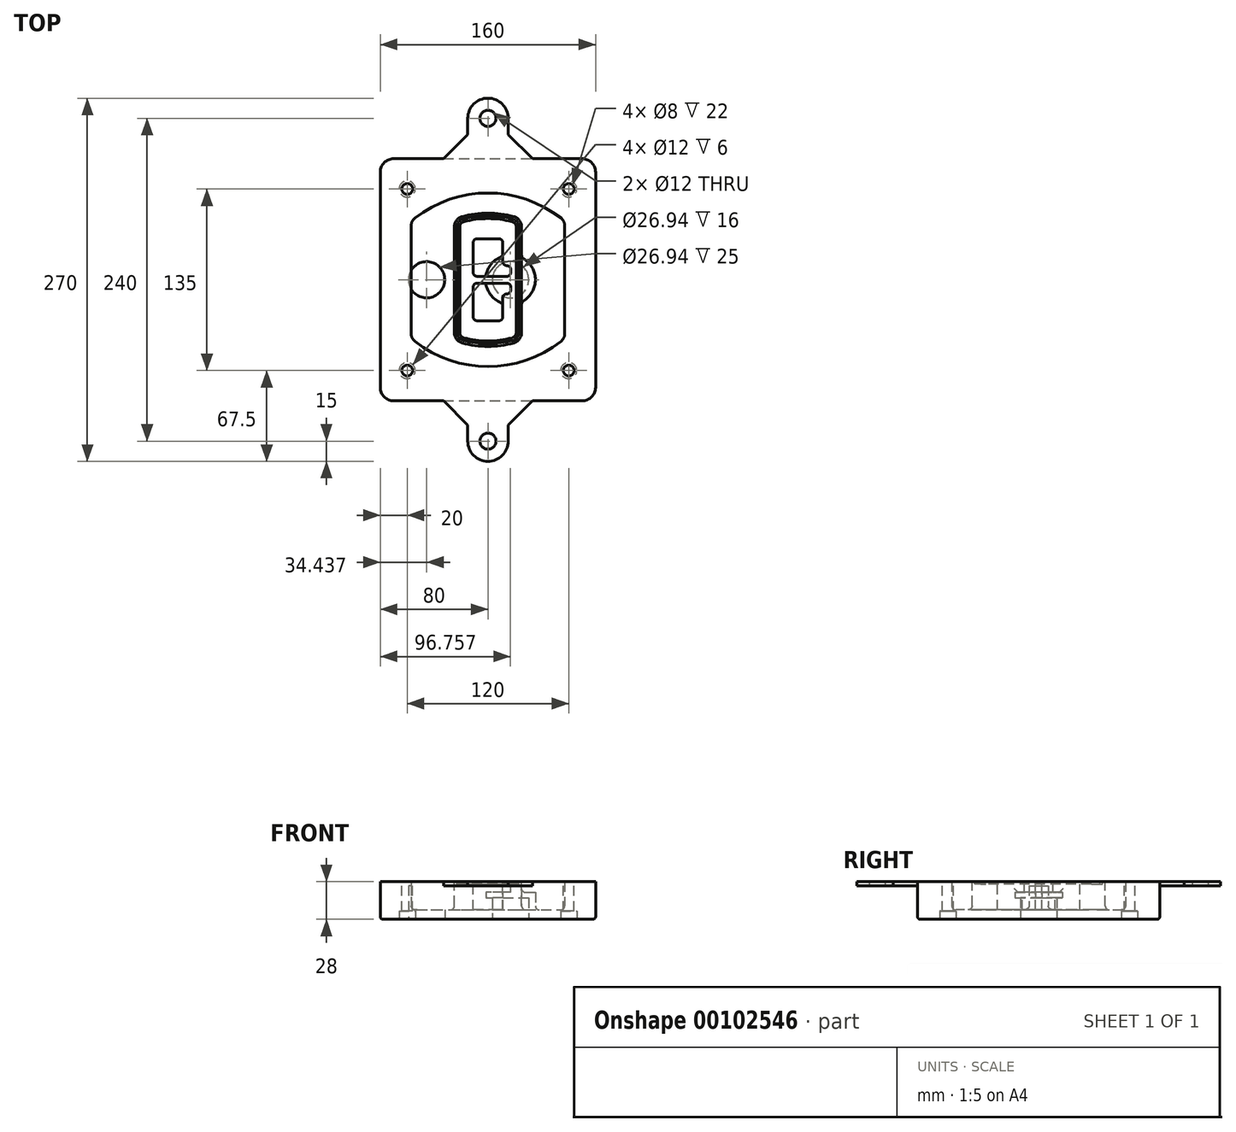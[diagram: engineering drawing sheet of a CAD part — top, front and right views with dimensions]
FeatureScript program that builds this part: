
annotation { "Feature Type Name" : "Feature", "Feature Type Description" : "" }
export const myFeature = defineFeature(function(context is Context, id is Id, definition is map)
    precondition{}
    {
        {
            var Q0;
            Q0=qCreatedBy(makeId("Top.planeOp"),FACE);
            var sketch = newSketch(context, id + "F0", { "sketchPlane" : qUnion([Q0])});
            skPoint(sketch, "E0.rect.middle", {"position": v(0, 0) * mm});
            skLineSegment(sketch, "E1.bottom", {"start": v(-70, -90) * mm, "end": v(70, -90) * mm});
            skLineSegment(sketch, "E1.top", {"start": v(-70, 90) * mm, "end": v(70, 90) * mm});
            skLineSegment(sketch, "E1.left", {"start": v(-80, -80) * mm, "end": v(-80, 80) * mm});
            skLineSegment(sketch, "E1.right", {"start": v(80, -80) * mm, "end": v(80, 80) * mm});
            skLineSegment(sketch, "E2", {"start": v(-80, 90) * mm, "end": v(80, -90) * mm, "construction": true});
            skLineSegment(sketch, "E3", {"start": v(80, 90) * mm, "end": v(-80, -90) * mm, "construction": true});
            skCircle(sketch, "E4", {"center": v(-60, 67.5) * mm, "radius": 4 * mm});
            skCircle(sketch, "E5", {"center": v(60, 67.5) * mm, "radius": 4 * mm});
            skCircle(sketch, "E6", {"center": v(60, -67.5) * mm, "radius": 4 * mm});
            skCircle(sketch, "E7", {"center": v(-60, -67.5) * mm, "radius": 4 * mm});
            skLineSegment(sketch, "E8", {"start": v(-60, 67.5) * mm, "end": v(60, 67.5) * mm, "construction": true});
            skLineSegment(sketch, "E9", {"start": v(60, 67.5) * mm, "end": v(60, -67.5) * mm, "construction": true});
            skLineSegment(sketch, "E10", {"start": v(60, -67.5) * mm, "end": v(-60, -67.5) * mm, "construction": true});
            skLineSegment(sketch, "E11", {"start": v(-60, -67.5) * mm, "end": v(-60, 67.5) * mm, "construction": true});
            skLineSegment(sketch, "E12", {"start": v(-60, 40.3) * mm, "end": v(-60, -40.3) * mm});
            skLineSegment(sketch, "E13", {"start": v(60, 40.3) * mm, "end": v(60, -40.3) * mm});
            skArc(sketch, "E14", {"start": v(56.15, 48.18) * mm, "mid": v(0, 67.5) * mm, "end": v(-56.15, 48.18) * mm});
            skArc(sketch, "E15", {"start": v(-56.15, -48.18) * mm, "mid": v(0, -67.5) * mm, "end": v(56.15, -48.18) * mm});
            skLineSegment(sketch, "E16", {"start": v(-60, 0) * mm, "end": v(60, 0) * mm, "construction": true});
            skPoint(sketch, "E17.visualSharp", {"position": v(-60, -45) * mm});
            skArc(sketch, "E17.filletArc", {"start": v(-60, -40.3) * mm, "mid": v(-58.99, -44.68) * mm, "end": v(-56.15, -48.18) * mm});
            skPoint(sketch, "E18.visualSharp", {"position": v(-60, 45) * mm});
            skArc(sketch, "E18.filletArc", {"start": v(-56.15, 48.18) * mm, "mid": v(-58.99, 44.68) * mm, "end": v(-60, 40.3) * mm});
            skPoint(sketch, "E19.visualSharp", {"position": v(60, 45) * mm});
            skArc(sketch, "E19.filletArc", {"start": v(60, 40.3) * mm, "mid": v(58.99, 44.68) * mm, "end": v(56.15, 48.18) * mm});
            skPoint(sketch, "E20.visualSharp", {"position": v(60, -45) * mm});
            skArc(sketch, "E20.filletArc", {"start": v(56.15, -48.18) * mm, "mid": v(58.99, -44.68) * mm, "end": v(60, -40.3) * mm});
            skPoint(sketch, "E21.visualSharp", {"position": v(-80, 90) * mm});
            skArc(sketch, "E21.filletArc", {"start": v(-70, 90) * mm, "mid": v(-77.07, 87.07) * mm, "end": v(-80, 80) * mm});
            skPoint(sketch, "E22.visualSharp", {"position": v(80, 90) * mm});
            skArc(sketch, "E22.filletArc", {"start": v(80, 80) * mm, "mid": v(77.07, 87.07) * mm, "end": v(70, 90) * mm});
            skPoint(sketch, "E23.visualSharp", {"position": v(80, -90) * mm});
            skArc(sketch, "E23.filletArc", {"start": v(70, -90) * mm, "mid": v(77.07, -87.07) * mm, "end": v(80, -80) * mm});
            skPoint(sketch, "E24.visualSharp", {"position": v(-80, -90) * mm});
            skArc(sketch, "E24.filletArc", {"start": v(-80, -80) * mm, "mid": v(-77.07, -87.07) * mm, "end": v(-70, -90) * mm});
            skArc(sketch, "E25.0", {"start": v(57, 40.3) * mm, "mid": v(56.3, 43.36) * mm, "end": v(54.3, 45.81) * mm});
            skLineSegment(sketch, "E25.1", {"start": v(57, 40.3) * mm, "end": v(57, -40.3) * mm});
            skArc(sketch, "E25.2", {"start": v(54.3, -45.81) * mm, "mid": v(56.3, -43.36) * mm, "end": v(57, -40.3) * mm});
            skArc(sketch, "E25.3", {"start": v(-54.3, -45.81) * mm, "mid": v(0, -64.5) * mm, "end": v(54.3, -45.81) * mm});
            skArc(sketch, "E25.4", {"start": v(-57, -40.3) * mm, "mid": v(-56.3, -43.36) * mm, "end": v(-54.3, -45.81) * mm});
            skArc(sketch, "E25.5", {"start": v(54.3, 45.81) * mm, "mid": v(0, 64.5) * mm, "end": v(-54.3, 45.81) * mm});
            skLineSegment(sketch, "E25.6", {"start": v(-57, 40.3) * mm, "end": v(-57, -40.3) * mm});
            skArc(sketch, "E25.7", {"start": v(-54.3, 45.81) * mm, "mid": v(-56.3, 43.36) * mm, "end": v(-57, 40.3) * mm});
            skArc(sketch, "E26.0", {"start": v(-58.62, 51.33) * mm, "mid": v(-62.58, 46.43) * mm, "end": v(-64, 40.3) * mm});
            skArc(sketch, "E26.1", {"start": v(58.62, 51.33) * mm, "mid": v(0, 71.5) * mm, "end": v(-58.62, 51.33) * mm});
            skArc(sketch, "E26.2", {"start": v(64, 40.3) * mm, "mid": v(62.58, 46.43) * mm, "end": v(58.62, 51.33) * mm});
            skLineSegment(sketch, "E26.3", {"start": v(64, 40.3) * mm, "end": v(64, -40.3) * mm});
            skArc(sketch, "E26.4", {"start": v(58.62, -51.33) * mm, "mid": v(62.58, -46.43) * mm, "end": v(64, -40.3) * mm});
            skLineSegment(sketch, "E26.5", {"start": v(-64, 40.3) * mm, "end": v(-64, -40.3) * mm});
            skArc(sketch, "E26.6", {"start": v(-58.62, -51.33) * mm, "mid": v(0, -71.5) * mm, "end": v(58.62, -51.33) * mm});
            skArc(sketch, "E26.7", {"start": v(-64, -40.3) * mm, "mid": v(-62.58, -46.43) * mm, "end": v(-58.62, -51.33) * mm});
            skSolve(sketch);
        }
        {
            var Q0;
            Q0=makeQuery(id+"F0.imprint","IMPRINT",FACE,{"disambiguationData":[TD([[makeQuery(id+"F0.imprint","IMPRINT",EDGE,{"derivedFrom":sQuery(id+"F0.wireOp",EDGE,"E1.bottom")}),1.0]])]});
            var Q1;
            Q1=makeQuery(id+"F0.imprint","IMPRINT",FACE,{"disambiguationData":[TD([[makeQuery(id+"F0.imprint","IMPRINT",EDGE,{"derivedFrom":sQuery(id+"F0.wireOp",EDGE,"E12")}),1.0]])]});
            var Q2;
            Q2=makeQuery(id+"F0.imprint","IMPRINT",FACE,{"disambiguationData":[TD([[makeQuery(id+"F0.imprint","IMPRINT",EDGE,{"derivedFrom":sQuery(id+"F0.wireOp",EDGE,"E25.0")}),1.0]])]});
            var Q3;
            Q3=makeQuery(id+"F0.imprint","IMPRINT",FACE,{"disambiguationData":[TD([[makeQuery(id+"F0.imprint","IMPRINT",EDGE,{"derivedFrom":sQuery(id+"F0.wireOp",EDGE,"E12")}),-1.0]])]});
            extrude(context, id + "F1", {"entities" : qUnion([Q0, Q1, Q2, Q3]), "oppositeDirection" : true, "depth" : 25 * mm});
        }
        {
            var Q0;
            Q0=makeQuery(id+"F0.imprint","IMPRINT",FACE,{"disambiguationData":[TD([[makeQuery(id+"F0.imprint","IMPRINT",EDGE,{"derivedFrom":sQuery(id+"F0.wireOp",EDGE,"E12")}),1.0]])]});
            extrude(context, id + "F2", {"entities" : qUnion([Q0]), "operationType" : NewBodyOperationType.ADD, "depth" : 3 * mm});
        }
        {
            var Q0;
            Q0=makeQuery(id+"F0.imprint","IMPRINT",FACE,{"disambiguationData":[TD([[makeQuery(id+"F0.imprint","IMPRINT",EDGE,{"derivedFrom":sQuery(id+"F0.wireOp",EDGE,"E25.0")}),1.0]])]});
            extrude(context, id + "F3", {"entities" : qUnion([Q0]), "operationType" : NewBodyOperationType.REMOVE, "oppositeDirection" : true, "depth" : 18 * mm});
        }
        {
            var Q0;
            Q0=makeQuery(id+"F2.opExtrude","CAP_FACE",FACE,{"disambiguationData":[OSD([sQuery(id+"F0.wireOp",EDGE,"E12"),sQuery(id+"F0.wireOp",EDGE,"E13"),sQuery(id+"F0.wireOp",EDGE,"E14"),sQuery(id+"F0.wireOp",EDGE,"E15"),sQuery(id+"F0.wireOp",EDGE,"E17.filletArc"),sQuery(id+"F0.wireOp",EDGE,"E18.filletArc"),sQuery(id+"F0.wireOp",EDGE,"E19.filletArc"),sQuery(id+"F0.wireOp",EDGE,"E20.filletArc"),sQuery(id+"F0.wireOp",EDGE,"E25.0"),sQuery(id+"F0.wireOp",EDGE,"E25.1"),sQuery(id+"F0.wireOp",EDGE,"E25.2"),sQuery(id+"F0.wireOp",EDGE,"E25.3"),sQuery(id+"F0.wireOp",EDGE,"E25.4"),sQuery(id+"F0.wireOp",EDGE,"E25.5"),sQuery(id+"F0.wireOp",EDGE,"E25.6"),sQuery(id+"F0.wireOp",EDGE,"E25.7")])],"isStart":false});
            var sketch = newSketch(context, id + "F4", { "sketchPlane" : qUnion([Q0])});
            skArc(sketch, "E27.0", {"start": v(-19.08, -46.97) * mm, "mid": v(0, -49.5) * mm, "end": v(19.08, -46.97) * mm});
            skArc(sketch, "E28.0", {"start": v(19.08, 46.97) * mm, "mid": v(0, 49.5) * mm, "end": v(-19.08, 46.97) * mm});
            skLineSegment(sketch, "E29", {"start": v(-25, 39.25) * mm, "end": v(-25, -39.25) * mm});
            skLineSegment(sketch, "E30", {"start": v(25, 39.25) * mm, "end": v(25, -39.25) * mm});
            skLineSegment(sketch, "E31", {"start": v(-25, 45.1) * mm, "end": v(25, 45.1) * mm, "construction": true});
            skLineSegment(sketch, "E32", {"start": v(-25, -45.1) * mm, "end": v(25, -45.1) * mm, "construction": true});
            skPoint(sketch, "E33.visualSharp", {"position": v(-25, 45.1) * mm});
            skArc(sketch, "E33.filletArc", {"start": v(-19.08, 46.97) * mm, "mid": v(-23.35, 44.11) * mm, "end": v(-25, 39.25) * mm});
            skPoint(sketch, "E34.visualSharp", {"position": v(25, 45.1) * mm});
            skArc(sketch, "E34.filletArc", {"start": v(25, 39.25) * mm, "mid": v(23.35, 44.11) * mm, "end": v(19.08, 46.97) * mm});
            skPoint(sketch, "E35.visualSharp", {"position": v(25, -45.1) * mm});
            skArc(sketch, "E35.filletArc", {"start": v(19.08, -46.97) * mm, "mid": v(23.35, -44.11) * mm, "end": v(25, -39.25) * mm});
            skPoint(sketch, "E36.visualSharp", {"position": v(-25, -45.1) * mm});
            skArc(sketch, "E36.filletArc", {"start": v(-25, -39.25) * mm, "mid": v(-23.35, -44.11) * mm, "end": v(-19.08, -46.97) * mm});
            skArc(sketch, "E37.0", {"start": v(54.3, 45.81) * mm, "mid": v(0, 64.5) * mm, "end": v(-54.3, 45.81) * mm});
            skArc(sketch, "E37.1", {"start": v(-54.3, 45.81) * mm, "mid": v(-56.3, 43.36) * mm, "end": v(-57, 40.3) * mm});
            skLineSegment(sketch, "E37.2", {"start": v(-57, 40.3) * mm, "end": v(-57, -40.3) * mm});
            skArc(sketch, "E37.3", {"start": v(-57, -40.3) * mm, "mid": v(-56.3, -43.36) * mm, "end": v(-54.3, -45.81) * mm});
            skArc(sketch, "E37.4", {"start": v(-54.3, -45.81) * mm, "mid": v(0, -64.5) * mm, "end": v(54.3, -45.81) * mm});
            skArc(sketch, "E37.5", {"start": v(54.3, -45.81) * mm, "mid": v(56.3, -43.36) * mm, "end": v(57, -40.3) * mm});
            skLineSegment(sketch, "E37.6", {"start": v(57, 40.3) * mm, "end": v(57, -40.3) * mm});
            skArc(sketch, "E37.7", {"start": v(57, 40.3) * mm, "mid": v(56.3, 43.36) * mm, "end": v(54.3, 45.81) * mm});
            skLineSegment(sketch, "E38.0", {"start": v(23, 39.25) * mm, "end": v(23, -39.25) * mm});
            skArc(sketch, "E38.1", {"start": v(18.56, -45.04) * mm, "mid": v(21.76, -42.9) * mm, "end": v(23, -39.25) * mm});
            skArc(sketch, "E38.2", {"start": v(-18.56, -45.04) * mm, "mid": v(0, -47.5) * mm, "end": v(18.56, -45.04) * mm});
            skArc(sketch, "E38.3", {"start": v(-23, -39.25) * mm, "mid": v(-21.76, -42.9) * mm, "end": v(-18.56, -45.04) * mm});
            skLineSegment(sketch, "E38.4", {"start": v(-23, 39.25) * mm, "end": v(-23, -39.25) * mm});
            skArc(sketch, "E38.5", {"start": v(23, 39.25) * mm, "mid": v(21.76, 42.9) * mm, "end": v(18.56, 45.04) * mm});
            skArc(sketch, "E38.6", {"start": v(-18.56, 45.04) * mm, "mid": v(-21.76, 42.9) * mm, "end": v(-23, 39.25) * mm});
            skArc(sketch, "E38.7", {"start": v(18.56, 45.04) * mm, "mid": v(0, 47.5) * mm, "end": v(-18.56, 45.04) * mm});
            skArc(sketch, "E39.0", {"start": v(21, 39.25) * mm, "mid": v(20.18, 41.68) * mm, "end": v(18.04, 43.1) * mm});
            skLineSegment(sketch, "E39.1", {"start": v(21, 39.25) * mm, "end": v(21, -39.25) * mm});
            skArc(sketch, "E39.2", {"start": v(18.04, -43.1) * mm, "mid": v(20.18, -41.68) * mm, "end": v(21, -39.25) * mm});
            skArc(sketch, "E39.3", {"start": v(-18.04, -43.1) * mm, "mid": v(0, -45.5) * mm, "end": v(18.04, -43.1) * mm});
            skArc(sketch, "E39.4", {"start": v(-21, -39.25) * mm, "mid": v(-20.18, -41.68) * mm, "end": v(-18.04, -43.1) * mm});
            skArc(sketch, "E39.5", {"start": v(18.04, 43.1) * mm, "mid": v(0, 45.5) * mm, "end": v(-18.04, 43.1) * mm});
            skLineSegment(sketch, "E39.6", {"start": v(-21, 39.25) * mm, "end": v(-21, -39.25) * mm});
            skArc(sketch, "E39.7", {"start": v(-18.04, 43.1) * mm, "mid": v(-20.18, 41.68) * mm, "end": v(-21, 39.25) * mm});
            skLineSegment(sketch, "E40", {"start": v(-25, 0) * mm, "end": v(25, 0) * mm, "construction": true});
            skLineSegment(sketch, "E41", {"start": v(-11, 5.5) * mm, "end": v(-11, 27.5) * mm});
            skLineSegment(sketch, "E42", {"start": v(-8, 30.5) * mm, "end": v(8, 30.5) * mm});
            skLineSegment(sketch, "E43", {"start": v(11, 27.5) * mm, "end": v(11, 13.5) * mm});
            skLineSegment(sketch, "E44", {"start": v(14, 10.5) * mm, "end": v(14, 10.5) * mm});
            skLineSegment(sketch, "E45", {"start": v(17, 7.5) * mm, "end": v(17, 5.5) * mm});
            skLineSegment(sketch, "E46", {"start": v(14, 2.5) * mm, "end": v(-8, 2.5) * mm});
            skPoint(sketch, "E47.visualSharp", {"position": v(-11, 30.5) * mm});
            skArc(sketch, "E47.filletArc", {"start": v(-8, 30.5) * mm, "mid": v(-10.12, 29.62) * mm, "end": v(-11, 27.5) * mm});
            skPoint(sketch, "E48.visualSharp", {"position": v(11, 30.5) * mm});
            skArc(sketch, "E48.filletArc", {"start": v(11, 27.5) * mm, "mid": v(10.12, 29.62) * mm, "end": v(8, 30.5) * mm});
            skPoint(sketch, "E49.visualSharp", {"position": v(11, 10.5) * mm});
            skArc(sketch, "E49.filletArc", {"start": v(11, 13.5) * mm, "mid": v(11.88, 11.38) * mm, "end": v(14, 10.5) * mm});
            skPoint(sketch, "E50.visualSharp", {"position": v(17, 10.5) * mm});
            skArc(sketch, "E50.filletArc", {"start": v(17, 7.5) * mm, "mid": v(16.12, 9.62) * mm, "end": v(14, 10.5) * mm});
            skPoint(sketch, "E51.visualSharp", {"position": v(17, 2.5) * mm});
            skArc(sketch, "E51.filletArc", {"start": v(14, 2.5) * mm, "mid": v(16.12, 3.38) * mm, "end": v(17, 5.5) * mm});
            skPoint(sketch, "E52.visualSharp", {"position": v(-11, 2.5) * mm});
            skArc(sketch, "E52.filletArc", {"start": v(-11, 5.5) * mm, "mid": v(-10.12, 3.38) * mm, "end": v(-8, 2.5) * mm});
            skLineSegment(sketch, "E53.0.MirrorCS", {"start": v(14, -2.5) * mm, "end": v(-8, -2.5) * mm});
            skArc(sketch, "E54.0.MirrorCS", {"start": v(-11, -5.5) * mm, "mid": v(-10.12, -3.38) * mm, "end": v(-8, -2.5) * mm});
            skLineSegment(sketch, "E55.0.MirrorCS", {"start": v(-11, -5.5) * mm, "end": v(-11, -27.5) * mm});
            skArc(sketch, "E56.0.MirrorCS", {"start": v(-8, -30.5) * mm, "mid": v(-10.12, -29.62) * mm, "end": v(-11, -27.5) * mm});
            skLineSegment(sketch, "E57.0.MirrorCS", {"start": v(-8, -30.5) * mm, "end": v(8, -30.5) * mm});
            skArc(sketch, "E58.0.MirrorCS", {"start": v(11, -27.5) * mm, "mid": v(10.12, -29.62) * mm, "end": v(8, -30.5) * mm});
            skLineSegment(sketch, "E59.0.MirrorCS", {"start": v(11, -27.5) * mm, "end": v(11, -13.5) * mm});
            skArc(sketch, "E60.0.MirrorCS", {"start": v(11, -13.5) * mm, "mid": v(11.88, -11.38) * mm, "end": v(14, -10.5) * mm});
            skArc(sketch, "E61.0.MirrorCS", {"start": v(17, -7.5) * mm, "mid": v(16.12, -9.62) * mm, "end": v(14, -10.5) * mm});
            skLineSegment(sketch, "E62.0.MirrorCS", {"start": v(17, -7.5) * mm, "end": v(17, -5.5) * mm});
            skArc(sketch, "E63.0.MirrorCS", {"start": v(14, -2.5) * mm, "mid": v(16.12, -3.38) * mm, "end": v(17, -5.5) * mm});
            skSolve(sketch);
        }
        {
            var Q0;
            Q0=makeQuery(id+"F4.imprint","IMPRINT",FACE,{"disambiguationData":[TD([[makeQuery(id+"F4.imprint","IMPRINT",EDGE,{"derivedFrom":sQuery(id+"F4.wireOp",EDGE,"E27.0")}),1.0]])]});
            var Q1;
            Q1=makeQuery(id+"F4.imprint","IMPRINT",FACE,{"disambiguationData":[TD([[makeQuery(id+"F4.imprint","IMPRINT",EDGE,{"derivedFrom":sQuery(id+"F4.wireOp",EDGE,"E38.0")}),-1.0]])]});
            var Q2;
            Q2=makeQuery(id+"F4.imprint","IMPRINT",FACE,{"disambiguationData":[TD([[makeQuery(id+"F4.imprint","IMPRINT",EDGE,{"derivedFrom":sQuery(id+"F4.wireOp",EDGE,"E39.0")}),1.0]])]});
            extrude(context, id + "F5", {"entities" : qUnion([Q0, Q1, Q2]), "operationType" : NewBodyOperationType.ADD, "endBound" : BoundingType.UP_TO_NEXT, "oppositeDirection" : true, "depth" : 25 * mm});
        }
        {
            var Q0;
            Q0=makeQuery(id+"F4.imprint","IMPRINT",FACE,{"disambiguationData":[TD([[makeQuery(id+"F4.imprint","IMPRINT",EDGE,{"derivedFrom":sQuery(id+"F4.wireOp",EDGE,"E38.0")}),-1.0]])]});
            extrude(context, id + "F6", {"entities" : qUnion([Q0]), "operationType" : NewBodyOperationType.REMOVE, "oppositeDirection" : true, "depth" : 2 * mm});
        }
        {
            var Q0;
            Q0=makeQuery(id+"F1.opExtrude","CAP_FACE",FACE,{"disambiguationData":[OSD([sQuery(id+"F0.wireOp",EDGE,"E1.bottom"),sQuery(id+"F0.wireOp",EDGE,"E1.top"),sQuery(id+"F0.wireOp",EDGE,"E1.left"),sQuery(id+"F0.wireOp",EDGE,"E1.right"),sQuery(id+"F0.wireOp",EDGE,"E4"),sQuery(id+"F0.wireOp",EDGE,"E5"),sQuery(id+"F0.wireOp",EDGE,"E6"),sQuery(id+"F0.wireOp",EDGE,"E7"),sQuery(id+"F0.wireOp",EDGE,"E21.filletArc"),sQuery(id+"F0.wireOp",EDGE,"E22.filletArc"),sQuery(id+"F0.wireOp",EDGE,"E23.filletArc"),sQuery(id+"F0.wireOp",EDGE,"E24.filletArc")])],"isStart":false});
            var sketch = newSketch(context, id + "F7", { "sketchPlane" : qUnion([Q0])});
            skCircle(sketch, "E64", {"center": v(16.76, 0) * mm, "radius": 13.47 * mm});
            skCircle(sketch, "E65", {"center": v(-45.56, 0) * mm, "radius": 13.47 * mm});
            skLineSegment(sketch, "E66", {"start": v(80, 0) * mm, "end": v(-80, 0) * mm});
            skCircle(sketch, "E67", {"center": v(16.76, 0) * mm, "radius": 18.47 * mm});
            skCircle(sketch, "E68", {"center": v(60, -67.5) * mm, "radius": 6 * mm});
            skCircle(sketch, "E69", {"center": v(-60, -67.5) * mm, "radius": 6 * mm});
            skCircle(sketch, "E70", {"center": v(-60, 67.5) * mm, "radius": 6 * mm});
            skCircle(sketch, "E71", {"center": v(60, 67.5) * mm, "radius": 6 * mm});
            skSolve(sketch);
        }
        {
            var Q0;
            {var subQ1=sQuery(id+"F7.wireOp",EDGE,"E66");var subQ4=sQuery(id+"F7.wireOp",EDGE,"E64");var subQ6=makeQuery(id+"F7.imprint","INTERSECT",VERTEX,{"disambiguationData":[OD(0.0)],"derivedFrom":[subQ4,subQ1]});Q0=makeQuery(id+"F7.imprint","IMPRINT",FACE,{"disambiguationData":[TD([[makeQuery(id+"F7.imprint","IMPRINT",EDGE,{"disambiguationData":[TD([[subQ6,-1.0]])],"derivedFrom":subQ4}),-1.0]])]});}
            var Q1;
            {var subQ0=sQuery(id+"F7.wireOp",EDGE,"E66");var subQ1=sQuery(id+"F7.wireOp",EDGE,"E64");var subQ3=makeQuery(id+"F7.imprint","INTERSECT",VERTEX,{"disambiguationData":[OD(0.0)],"derivedFrom":[subQ1,subQ0]});Q1=makeQuery(id+"F7.imprint","IMPRINT",FACE,{"disambiguationData":[TD([[makeQuery(id+"F7.imprint","IMPRINT",EDGE,{"disambiguationData":[TD([[subQ3,-1.0]])],"derivedFrom":subQ1}),1.0]])]});}
            var Q2;
            {var subQ0=sQuery(id+"F7.wireOp",EDGE,"E66");var subQ1=sQuery(id+"F7.wireOp",EDGE,"E64");var subQ3=makeQuery(id+"F7.imprint","INTERSECT",VERTEX,{"disambiguationData":[OD(0.0)],"derivedFrom":[subQ1,subQ0]});Q2=makeQuery(id+"F7.imprint","IMPRINT",FACE,{"disambiguationData":[TD([[makeQuery(id+"F7.imprint","IMPRINT",EDGE,{"disambiguationData":[TD([[subQ3,1.0]])],"derivedFrom":subQ1}),1.0]])]});}
            var Q3;
            {var subQ1=sQuery(id+"F7.wireOp",EDGE,"E66");var subQ4=sQuery(id+"F7.wireOp",EDGE,"E64");var subQ6=makeQuery(id+"F7.imprint","INTERSECT",VERTEX,{"disambiguationData":[OD(0.0)],"derivedFrom":[subQ4,subQ1]});Q3=makeQuery(id+"F7.imprint","IMPRINT",FACE,{"disambiguationData":[TD([[makeQuery(id+"F7.imprint","IMPRINT",EDGE,{"disambiguationData":[TD([[subQ6,1.0]])],"derivedFrom":subQ4}),-1.0]])]});}
            extrude(context, id + "F8", {"entities" : qUnion([Q0, Q1, Q2, Q3]), "operationType" : NewBodyOperationType.ADD, "oppositeDirection" : true, "depth" : 20 * mm});
        }
        {
            var Q0;
            {var subQ0=sQuery(id+"F7.wireOp",EDGE,"E66");var subQ1=sQuery(id+"F7.wireOp",EDGE,"E64");var subQ3=makeQuery(id+"F7.imprint","INTERSECT",VERTEX,{"disambiguationData":[OD(0.0)],"derivedFrom":[subQ1,subQ0]});Q0=makeQuery(id+"F7.imprint","IMPRINT",FACE,{"disambiguationData":[TD([[makeQuery(id+"F7.imprint","IMPRINT",EDGE,{"disambiguationData":[TD([[subQ3,-1.0]])],"derivedFrom":subQ1}),1.0]])]});}
            var Q1;
            {var subQ0=sQuery(id+"F7.wireOp",EDGE,"E66");var subQ1=sQuery(id+"F7.wireOp",EDGE,"E64");var subQ3=makeQuery(id+"F7.imprint","INTERSECT",VERTEX,{"disambiguationData":[OD(0.0)],"derivedFrom":[subQ1,subQ0]});Q1=makeQuery(id+"F7.imprint","IMPRINT",FACE,{"disambiguationData":[TD([[makeQuery(id+"F7.imprint","IMPRINT",EDGE,{"disambiguationData":[TD([[subQ3,1.0]])],"derivedFrom":subQ1}),1.0]])]});}
            extrude(context, id + "F9", {"entities" : qUnion([Q0, Q1]), "operationType" : NewBodyOperationType.REMOVE, "oppositeDirection" : true, "depth" : 16 * mm});
        }
        {
            var Q0;
            {var subQ0=sQuery(id+"F7.wireOp",EDGE,"E66");var subQ1=sQuery(id+"F7.wireOp",EDGE,"E65");var subQ3=makeQuery(id+"F7.imprint","INTERSECT",VERTEX,{"disambiguationData":[OD(0.0)],"derivedFrom":[subQ1,subQ0]});Q0=makeQuery(id+"F7.imprint","IMPRINT",FACE,{"disambiguationData":[TD([[makeQuery(id+"F7.imprint","IMPRINT",EDGE,{"disambiguationData":[TD([[subQ3,-1.0]])],"derivedFrom":subQ1}),1.0]])]});}
            var Q1;
            {var subQ0=sQuery(id+"F7.wireOp",EDGE,"E66");var subQ1=sQuery(id+"F7.wireOp",EDGE,"E65");var subQ3=makeQuery(id+"F7.imprint","INTERSECT",VERTEX,{"disambiguationData":[OD(0.0)],"derivedFrom":[subQ1,subQ0]});Q1=makeQuery(id+"F7.imprint","IMPRINT",FACE,{"disambiguationData":[TD([[makeQuery(id+"F7.imprint","IMPRINT",EDGE,{"disambiguationData":[TD([[subQ3,1.0]])],"derivedFrom":subQ1}),1.0]])]});}
            extrude(context, id + "F10", {"entities" : qUnion([Q0, Q1]), "operationType" : NewBodyOperationType.REMOVE, "oppositeDirection" : true, "depth" : 25 * mm});
        }
        {
            var Q0;
            Q0=makeQuery(id+"F7.imprint","IMPRINT",FACE,{"disambiguationData":[TD([[makeQuery(id+"F7.imprint","IMPRINT",EDGE,{"derivedFrom":sQuery(id+"F7.wireOp",EDGE,"E68")}),1.0]])]});
            var Q1;
            Q1=makeQuery(id+"F7.imprint","IMPRINT",FACE,{"disambiguationData":[TD([[makeQuery(id+"F7.imprint","IMPRINT",EDGE,{"derivedFrom":makeQuery(id+"F1.opExtrude","CAP_EDGE",EDGE,{"disambiguationData":[OSD([sQuery(id+"F0.wireOp",EDGE,"E5")])],"isStart":false})}),-1.0]])]});
            var Q2;
            Q2=makeQuery(id+"F7.imprint","IMPRINT",FACE,{"disambiguationData":[TD([[makeQuery(id+"F7.imprint","IMPRINT",EDGE,{"derivedFrom":sQuery(id+"F7.wireOp",EDGE,"E69")}),1.0]])]});
            var Q3;
            Q3=makeQuery(id+"F7.imprint","IMPRINT",FACE,{"disambiguationData":[TD([[makeQuery(id+"F7.imprint","IMPRINT",EDGE,{"derivedFrom":makeQuery(id+"F1.opExtrude","CAP_EDGE",EDGE,{"disambiguationData":[OSD([sQuery(id+"F0.wireOp",EDGE,"E4")])],"isStart":false})}),-1.0]])]});
            var Q4;
            Q4=makeQuery(id+"F7.imprint","IMPRINT",FACE,{"disambiguationData":[TD([[makeQuery(id+"F7.imprint","IMPRINT",EDGE,{"derivedFrom":sQuery(id+"F7.wireOp",EDGE,"E70")}),1.0]])]});
            var Q5;
            Q5=makeQuery(id+"F7.imprint","IMPRINT",FACE,{"disambiguationData":[TD([[makeQuery(id+"F7.imprint","IMPRINT",EDGE,{"derivedFrom":makeQuery(id+"F1.opExtrude","CAP_EDGE",EDGE,{"disambiguationData":[OSD([sQuery(id+"F0.wireOp",EDGE,"E7")])],"isStart":false})}),-1.0]])]});
            var Q6;
            Q6=makeQuery(id+"F7.imprint","IMPRINT",FACE,{"disambiguationData":[TD([[makeQuery(id+"F7.imprint","IMPRINT",EDGE,{"derivedFrom":sQuery(id+"F7.wireOp",EDGE,"E71")}),1.0]])]});
            var Q7;
            Q7=makeQuery(id+"F7.imprint","IMPRINT",FACE,{"disambiguationData":[TD([[makeQuery(id+"F7.imprint","IMPRINT",EDGE,{"derivedFrom":makeQuery(id+"F1.opExtrude","CAP_EDGE",EDGE,{"disambiguationData":[OSD([sQuery(id+"F0.wireOp",EDGE,"E6")])],"isStart":false})}),-1.0]])]});
            extrude(context, id + "F11", {"entities" : qUnion([Q0, Q1, Q2, Q3, Q4, Q5, Q6, Q7]), "operationType" : NewBodyOperationType.REMOVE, "oppositeDirection" : true, "depth" : 6 * mm});
        }
        {
            var Q0;
            Q0=makeQuery(id+"F9.boolean.opBoolean","COPY",FACE,{"derivedFrom":makeQuery(id+"F9.opExtrude","CAP_FACE",FACE,{"disambiguationData":[OSD([sQuery(id+"F7.wireOp",EDGE,"E64")])],"isStart":false})});
            var sketch = newSketch(context, id + "F12", { "sketchPlane" : qUnion([Q0])});
            skArc(sketch, "E72.0", {"start": v(11, 17.55) * mm, "mid": v(2.57, 11.82) * mm, "end": v(-1.54, 2.5) * mm});
            skArc(sketch, "E72.1", {"start": v(-1.54, -2.5) * mm, "mid": v(2.57, -11.82) * mm, "end": v(11, -17.55) * mm});
            skLineSegment(sketch, "E73", {"start": v(-1.54, -2.5) * mm, "end": v(14, -2.5) * mm});
            skLineSegment(sketch, "E74.0", {"start": v(14, 2.5) * mm, "end": v(-1.54, 2.5) * mm});
            skArc(sketch, "E74.1", {"start": v(14, 2.5) * mm, "mid": v(16.12, 3.38) * mm, "end": v(17, 5.5) * mm});
            skLineSegment(sketch, "E74.2", {"start": v(17, 7.5) * mm, "end": v(17, 5.5) * mm});
            skArc(sketch, "E74.3", {"start": v(17, 7.5) * mm, "mid": v(16.12, 9.62) * mm, "end": v(14, 10.5) * mm});
            skArc(sketch, "E74.4", {"start": v(11, 13.5) * mm, "mid": v(11.88, 11.38) * mm, "end": v(14, 10.5) * mm});
            skLineSegment(sketch, "E74.5", {"start": v(11, 17.55) * mm, "end": v(11, 13.5) * mm});
            skLineSegment(sketch, "E74.7", {"start": v(14, -2.5) * mm, "end": v(-1.54, -2.5) * mm});
            skArc(sketch, "E74.8", {"start": v(14, -2.5) * mm, "mid": v(16.12, -3.38) * mm, "end": v(17, -5.5) * mm});
            skLineSegment(sketch, "E74.9", {"start": v(17, -7.5) * mm, "end": v(17, -5.5) * mm});
            skArc(sketch, "E74.10", {"start": v(17, -7.5) * mm, "mid": v(16.12, -9.62) * mm, "end": v(14, -10.5) * mm});
            skArc(sketch, "E74.11", {"start": v(11, -13.5) * mm, "mid": v(11.88, -11.38) * mm, "end": v(14, -10.5) * mm});
            skLineSegment(sketch, "E74.12", {"start": v(11, -17.55) * mm, "end": v(11, -13.5) * mm});
            skPoint(sketch, "E75.orphan", {"position": v(11, -27.5) * mm});
            skPoint(sketch, "E76.orphan", {"position": v(-8, -2.5) * mm});
            skPoint(sketch, "E77.orphan", {"position": v(-8, 2.5) * mm});
            skPoint(sketch, "E78.orphan", {"position": v(11, 27.5) * mm});
            skSolve(sketch);
        }
        {
            var Q0;
            {var subQ7=sQuery(id+"F12.wireOp",EDGE,"E72.0");var subQ14=sQuery(id+"F12.wireOp",EDGE,"E72.1");var subQ16=sQuery(id+"F12.wireOp",EDGE,"E74.1");var subQ18=sQuery(id+"F12.wireOp",EDGE,"E74.8");Q0=qUnion([makeQuery(id+"F12.imprint","IMPRINT",FACE,{"disambiguationData":[TD([[makeQuery(id+"F12.imprint","IMPRINT",EDGE,{"derivedFrom":subQ7}),1.0]])]}),makeQuery(id+"F12.imprint","IMPRINT",FACE,{"disambiguationData":[TD([[makeQuery(id+"F12.imprint","IMPRINT",EDGE,{"derivedFrom":subQ14}),1.0]])]}),makeQuery(id+"F12.imprint","IMPRINT",FACE,{"disambiguationData":[TD([[makeQuery(id+"F12.imprint","IMPRINT",EDGE,{"derivedFrom":subQ16}),1.0]])]}),makeQuery(id+"F12.imprint","IMPRINT",FACE,{"disambiguationData":[TD([[makeQuery(id+"F12.imprint","IMPRINT",EDGE,{"derivedFrom":subQ18}),-1.0]])]})]);}
            var Q1;
            Q1=makeQuery(id+"F5.boolean.opBoolean","SPLIT",FACE,{"disambiguationData":[TD([makeQuery(id+"F5.opExtrude","SWEPT_FACE",FACE,{"disambiguationData":[OSD([sQuery(id+"F4.wireOp",EDGE,"E41")])]})])],"derivedFrom":makeQuery(id+"F3.boolean.opBoolean","COPY",FACE,{"derivedFrom":makeQuery(id+"F3.opExtrude","CAP_FACE",FACE,{"disambiguationData":[OSD([sQuery(id+"F0.wireOp",EDGE,"E25.0"),sQuery(id+"F0.wireOp",EDGE,"E25.1"),sQuery(id+"F0.wireOp",EDGE,"E25.2"),sQuery(id+"F0.wireOp",EDGE,"E25.3"),sQuery(id+"F0.wireOp",EDGE,"E25.4"),sQuery(id+"F0.wireOp",EDGE,"E25.5"),sQuery(id+"F0.wireOp",EDGE,"E25.6"),sQuery(id+"F0.wireOp",EDGE,"E25.7")])],"isStart":false})})});
            extrude(context, id + "F13", {"entities" : qUnion([Q0]), "operationType" : NewBodyOperationType.REMOVE, "endBound" : BoundingType.UP_TO_SURFACE, "endBoundEntityFace" : qUnion([Q1]), "depth" : 25 * mm});
        }
        {
            var Q0;
            Q0=makeQuery(id+"F3.boolean.opBoolean","COPY",EDGE,{"derivedFrom":makeQuery(id+"F3.opExtrude","CAP_EDGE",EDGE,{"disambiguationData":[OSD([sQuery(id+"F0.wireOp",EDGE,"E25.6")])],"isStart":false})});
            var Q1;
            Q1=makeQuery(id+"F8.boolean.opBoolean","INTERSECT",EDGE,{"derivedFrom":[makeQuery(id+"F5.opExtrude","SWEPT_FACE",FACE,{"disambiguationData":[OSD([sQuery(id+"F4.wireOp",EDGE,"E30")])]}),makeQuery(id+"F8.opExtrude","CAP_FACE",FACE,{"disambiguationData":[OSD([sQuery(id+"F7.wireOp",EDGE,"E67")])],"isStart":false})]});
            var Q2;
            Q2=makeQuery(id+"F8.boolean.opBoolean","INTERSECT",EDGE,{"disambiguationData":[OD(1.0)],"derivedFrom":[makeQuery(id+"F5.opExtrude","SWEPT_FACE",FACE,{"disambiguationData":[OSD([sQuery(id+"F4.wireOp",EDGE,"E30")])]}),makeQuery(id+"F8.opExtrude","SWEPT_FACE",FACE,{"disambiguationData":[OSD([sQuery(id+"F7.wireOp",EDGE,"E67")])]})]});
            var Q3;
            {var subQ0=sQuery(id+"F4.wireOp",EDGE,"E30");Q3=makeQuery(id+"F8.boolean.opBoolean","SPLIT",EDGE,{"disambiguationData":[TD([makeQuery(id+"F5.opExtrude","SWEPT_FACE",FACE,{"disambiguationData":[OSD([sQuery(id+"F4.wireOp",EDGE,"E35.filletArc")])]})])],"derivedFrom":makeQuery(id+"F5.opExtrude","CAP_EDGE",EDGE,{"disambiguationData":[OSD([subQ0])],"isStart":false})});}
            var Q4;
            {var subQ0=sQuery(id+"F0.wireOp",EDGE,"E25.7");var subQ1=sQuery(id+"F0.wireOp",EDGE,"E25.1");var subQ2=sQuery(id+"F0.wireOp",EDGE,"E25.6");var subQ3=sQuery(id+"F0.wireOp",EDGE,"E25.5");var subQ4=sQuery(id+"F0.wireOp",EDGE,"E25.4");var subQ5=sQuery(id+"F0.wireOp",EDGE,"E25.0");var subQ6=sQuery(id+"F0.wireOp",EDGE,"E25.2");var subQ7=sQuery(id+"F0.wireOp",EDGE,"E25.3");Q4=makeQuery(id+"F8.boolean.opBoolean","INTERSECT",EDGE,{"derivedFrom":[makeQuery(id+"F5.boolean.opBoolean","SPLIT",FACE,{"disambiguationData":[TD([makeQuery(id+"F2.opExtrude","SWEPT_FACE",FACE,{"disambiguationData":[OSD([subQ5])]})])],"derivedFrom":makeQuery(id+"F3.boolean.opBoolean","COPY",FACE,{"derivedFrom":makeQuery(id+"F3.opExtrude","CAP_FACE",FACE,{"disambiguationData":[OSD([subQ5,subQ1,subQ6,subQ7,subQ4,subQ3,subQ2,subQ0])],"isStart":false})})}),makeQuery(id+"F8.opExtrude","SWEPT_FACE",FACE,{"disambiguationData":[OSD([sQuery(id+"F7.wireOp",EDGE,"E67")])]})]});}
            var Q5;
            Q5=makeQuery(id+"F8.boolean.opBoolean","INTERSECT",EDGE,{"disambiguationData":[OD(0.0)],"derivedFrom":[makeQuery(id+"F5.opExtrude","SWEPT_FACE",FACE,{"disambiguationData":[OSD([sQuery(id+"F4.wireOp",EDGE,"E30")])]}),makeQuery(id+"F8.opExtrude","SWEPT_FACE",FACE,{"disambiguationData":[OSD([sQuery(id+"F7.wireOp",EDGE,"E67")])]})]});
            fillet(context, id + "F14", {"entities" : qUnion([Q0, Q1, Q2, Q3, Q4, Q5]), "radius" : 3 * mm, "tangentPropagation" : true, "allowEdgeOverflow" : false});
        }
        {
            var Q0;
            Q0=makeQuery(id+"F1.opExtrude","CAP_EDGE",EDGE,{"disambiguationData":[OSD([sQuery(id+"F0.wireOp",EDGE,"E1.bottom")])],"isStart":false});
            fillet(context, id + "F15", {"entities" : qUnion([Q0]), "radius" : 2 * mm, "tangentPropagation" : true, "allowEdgeOverflow" : false});
        }
        {
            var Q0;
            {var subQ0=sQuery(id+"F0.wireOp",EDGE,"E22.filletArc");var subQ1=sQuery(id+"F0.wireOp",EDGE,"E7");var subQ2=sQuery(id+"F0.wireOp",EDGE,"E6");var subQ3=sQuery(id+"F0.wireOp",EDGE,"E5");var subQ4=sQuery(id+"F0.wireOp",EDGE,"E4");var subQ5=sQuery(id+"F0.wireOp",EDGE,"E1.bottom");var subQ6=sQuery(id+"F0.wireOp",EDGE,"E21.filletArc");var subQ7=sQuery(id+"F0.wireOp",EDGE,"E1.top");var subQ8=sQuery(id+"F0.wireOp",EDGE,"E1.left");var subQ9=sQuery(id+"F0.wireOp",EDGE,"E1.right");var subQ10=sQuery(id+"F0.wireOp",EDGE,"E23.filletArc");var subQ11=sQuery(id+"F0.wireOp",EDGE,"E24.filletArc");Q0=makeQuery(id+"F2.boolean.opBoolean","SPLIT",FACE,{"disambiguationData":[TD([makeQuery(id+"F1.opExtrude","SWEPT_FACE",FACE,{"disambiguationData":[OSD([subQ5])]})])],"derivedFrom":makeQuery(id+"F1.opExtrude","CAP_FACE",FACE,{"disambiguationData":[OSD([subQ5,subQ7,subQ8,subQ9,subQ4,subQ3,subQ2,subQ1,subQ6,subQ0,subQ10,subQ11])],"isStart":true})});}
            var sketch = newSketch(context, id + "F16", { "sketchPlane" : qUnion([Q0])});
            skLineSegment(sketch, "E79", {"start": v(0, 90) * mm, "end": v(0, 120) * mm, "construction": true});
            skLineSegment(sketch, "E80", {"start": v(-33, 90) * mm, "end": v(-15, 108) * mm});
            skLineSegment(sketch, "E81", {"start": v(33, 90) * mm, "end": v(15, 108) * mm});
            skLineSegment(sketch, "E82", {"start": v(-15, 108) * mm, "end": v(-15, 120) * mm});
            skLineSegment(sketch, "E83", {"start": v(15, 108) * mm, "end": v(15, 120) * mm});
            skArc(sketch, "E84", {"start": v(15, 120) * mm, "mid": v(0, 135) * mm, "end": v(-15, 120) * mm});
            skCircle(sketch, "E85", {"center": v(0, 120) * mm, "radius": 6 * mm});
            skLineSegment(sketch, "E86", {"start": v(-80, 0) * mm, "end": v(76.86, 0) * mm, "construction": true});
            skPoint(sketch, "E86.endSnap0", {"position": v(80, 0) * mm});
            skLineSegment(sketch, "E87.MirrorCS", {"start": v(-33, -90) * mm, "end": v(-15, -108) * mm});
            skLineSegment(sketch, "E88.MirrorCS", {"start": v(-15, -108) * mm, "end": v(-15, -120) * mm});
            skArc(sketch, "E89.MirrorCS", {"start": v(15, -120) * mm, "mid": v(0, -135) * mm, "end": v(-15, -120) * mm});
            skLineSegment(sketch, "E90.MirrorCS", {"start": v(15, -108) * mm, "end": v(15, -120) * mm});
            skLineSegment(sketch, "E91.MirrorCS", {"start": v(33, -90) * mm, "end": v(15, -108) * mm});
            skCircle(sketch, "E92.MirrorC", {"center": v(0, -120) * mm, "radius": 6 * mm});
            skSolve(sketch);
        }
        {
            var Q0;
            {var subQ0=sQuery(id+"F16.wireOp",EDGE,"E87.MirrorCS");Q0=makeQuery(id+"F16.imprint","IMPRINT",FACE,{"disambiguationData":[TD([[makeQuery(id+"F16.imprint","IMPRINT",EDGE,{"derivedFrom":subQ0}),1.0]])]});}
            var Q1;
            {var subQ0=sQuery(id+"F16.wireOp",EDGE,"E80");Q1=makeQuery(id+"F16.imprint","IMPRINT",FACE,{"disambiguationData":[TD([[makeQuery(id+"F16.imprint","IMPRINT",EDGE,{"derivedFrom":subQ0}),-1.0]])]});}
            var Q2;
            Q2=makeQuery(id+"F16.imprint","IMPRINT",FACE,{"disambiguationData":[TD([[makeQuery(id+"F16.imprint","IMPRINT",EDGE,{"derivedFrom":makeQuery(id+"F1.opExtrude","CAP_EDGE",EDGE,{"disambiguationData":[OSD([sQuery(id+"F0.wireOp",EDGE,"E1.left")])],"isStart":true})}),-1.0]])]});
            var Q3;
            {var subQ0=sQuery(id+"F4.wireOp",EDGE,"E63.0.MirrorCS");var subQ1=sQuery(id+"F4.wireOp",EDGE,"E62.0.MirrorCS");var subQ2=sQuery(id+"F4.wireOp",EDGE,"E61.0.MirrorCS");var subQ3=sQuery(id+"F4.wireOp",EDGE,"E60.0.MirrorCS");var subQ4=sQuery(id+"F4.wireOp",EDGE,"E59.0.MirrorCS");var subQ5=sQuery(id+"F4.wireOp",EDGE,"E58.0.MirrorCS");var subQ6=sQuery(id+"F4.wireOp",EDGE,"E57.0.MirrorCS");var subQ7=sQuery(id+"F4.wireOp",EDGE,"E56.0.MirrorCS");var subQ8=sQuery(id+"F4.wireOp",EDGE,"E55.0.MirrorCS");var subQ9=sQuery(id+"F4.wireOp",EDGE,"E54.0.MirrorCS");var subQ10=sQuery(id+"F4.wireOp",EDGE,"E53.0.MirrorCS");var subQ11=sQuery(id+"F4.wireOp",EDGE,"E52.filletArc");var subQ12=sQuery(id+"F4.wireOp",EDGE,"E45");var subQ13=sQuery(id+"F4.wireOp",EDGE,"E43");var subQ14=sQuery(id+"F4.wireOp",EDGE,"E42");var subQ15=sQuery(id+"F4.wireOp",EDGE,"E41");var subQ16=sQuery(id+"F4.wireOp",EDGE,"E46");var subQ17=sQuery(id+"F4.wireOp",EDGE,"E47.filletArc");var subQ18=sQuery(id+"F4.wireOp",EDGE,"E48.filletArc");var subQ19=sQuery(id+"F4.wireOp",EDGE,"E49.filletArc");var subQ20=sQuery(id+"F4.wireOp",EDGE,"E50.filletArc");var subQ21=sQuery(id+"F4.wireOp",EDGE,"E51.filletArc");Q3=makeQuery(id+"F6.boolean.opBoolean","SPLIT",FACE,{"disambiguationData":[TD([makeQuery(id+"F5.opExtrude","SWEPT_FACE",FACE,{"disambiguationData":[OSD([subQ15])]})])],"derivedFrom":makeQuery(id+"F5.opExtrude","CAP_FACE",FACE,{"disambiguationData":[OSD([sQuery(id+"F4.wireOp",EDGE,"E27.0"),sQuery(id+"F4.wireOp",EDGE,"E28.0"),sQuery(id+"F4.wireOp",EDGE,"E29"),sQuery(id+"F4.wireOp",EDGE,"E30"),sQuery(id+"F4.wireOp",EDGE,"E33.filletArc"),sQuery(id+"F4.wireOp",EDGE,"E34.filletArc"),sQuery(id+"F4.wireOp",EDGE,"E35.filletArc"),sQuery(id+"F4.wireOp",EDGE,"E36.filletArc"),subQ15,subQ14,subQ13,subQ12,subQ16,subQ17,subQ18,subQ19,subQ20,subQ21,subQ11,subQ10,subQ9,subQ8,subQ7,subQ6,subQ5,subQ4,subQ3,subQ2,subQ1,subQ0])],"isStart":true})});}
            extrude(context, id + "F17", {"entities" : qUnion([Q0, Q1, Q2]), "operationType" : NewBodyOperationType.ADD, "endBound" : BoundingType.UP_TO_SURFACE, "endBoundEntityFace" : qUnion([Q3]), "depth" : 25 * mm});
        }
    });
